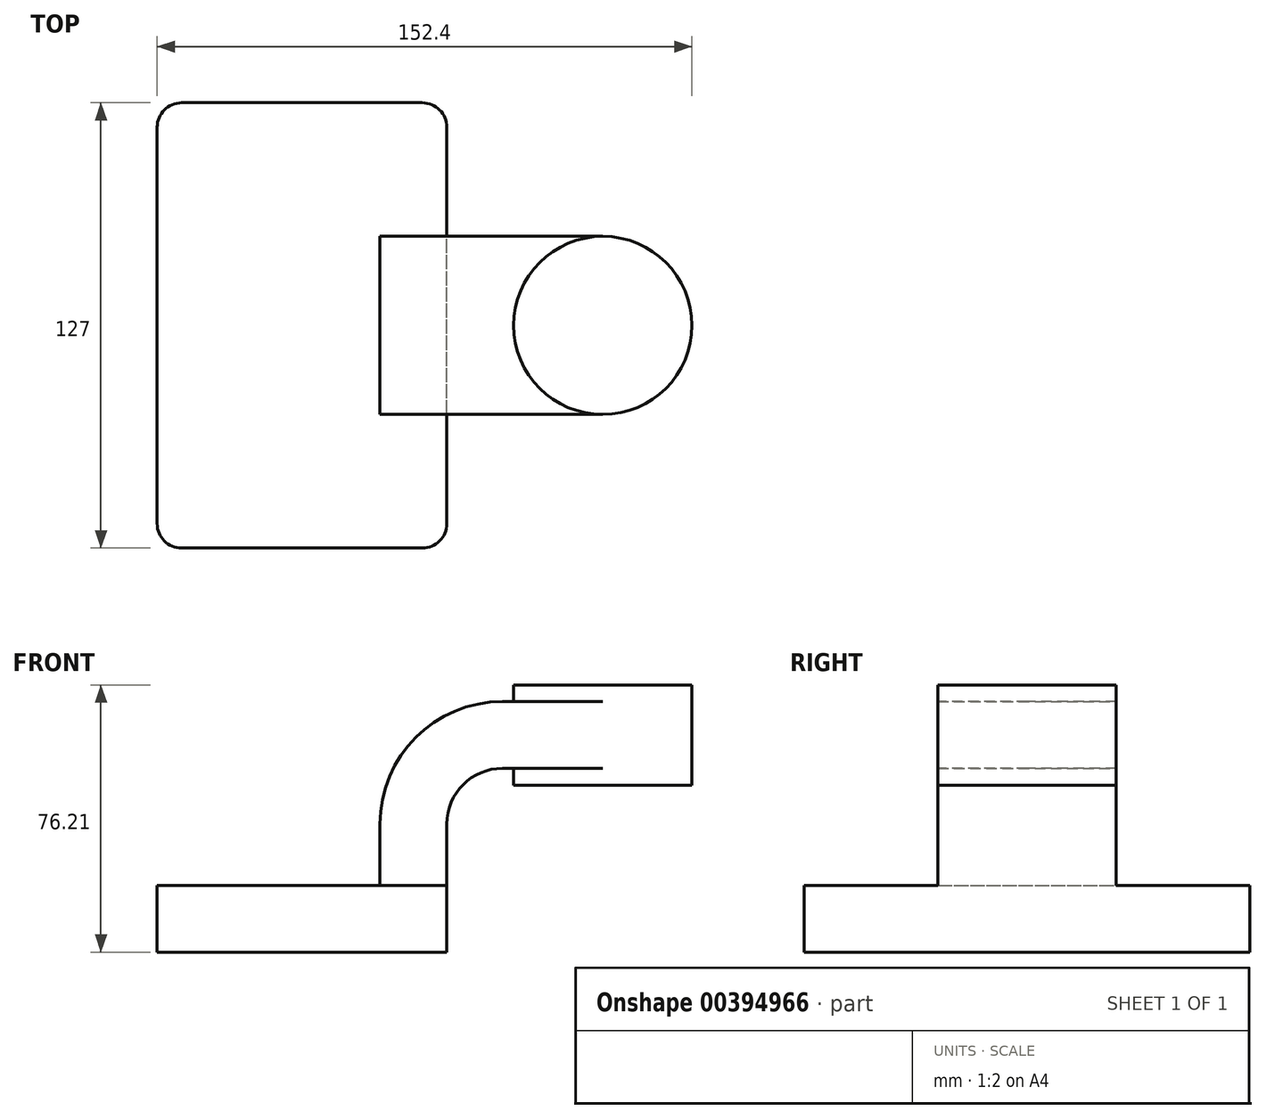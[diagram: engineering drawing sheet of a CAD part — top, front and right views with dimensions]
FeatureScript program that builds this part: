
annotation { "Feature Type Name" : "Feature", "Feature Type Description" : "" }
export const myFeature = defineFeature(function(context is Context, id is Id, definition is map)
    precondition{}
    {
        {
            var Q0;
            Q0=qCreatedBy(makeId("Front.planeOp"),FACE);
            var sketch = newSketch(context, id + "F0", { "sketchPlane" : qUnion([Q0])});
            skLineSegment(sketch, "E0.bottom", {"start": v(-41.28, 9.52) * mm, "end": v(41.27, 9.53) * mm});
            skLineSegment(sketch, "E0.top", {"start": v(-41.28, -9.52) * mm, "end": v(41.28, -9.52) * mm});
            skLineSegment(sketch, "E0.left", {"start": v(-41.28, 9.52) * mm, "end": v(-41.28, -9.53) * mm});
            skLineSegment(sketch, "E0.right", {"start": v(41.27, 9.53) * mm, "end": v(41.28, -9.52) * mm});
            skPoint(sketch, "E0.middle", {"position": v(0, 0) * mm});
            skLineSegment(sketch, "E1.bottom", {"start": v(60.32, 38.1) * mm, "end": v(111.12, 38.1) * mm});
            skLineSegment(sketch, "E1.top", {"start": v(60.32, 66.67) * mm, "end": v(111.12, 66.67) * mm});
            skLineSegment(sketch, "E1.left", {"start": v(60.32, 38.1) * mm, "end": v(60.32, 66.67) * mm});
            skLineSegment(sketch, "E1.right", {"start": v(111.12, 38.1) * mm, "end": v(111.12, 66.67) * mm});
            skPoint(sketch, "E1.middle", {"position": v(85.72, 52.39) * mm});
            skLineSegment(sketch, "E2", {"start": v(41.27, 9.53) * mm, "end": v(41.27, 27) * mm});
            skArc(sketch, "E3", {"start": v(41.27, 27) * mm, "mid": v(45.92, 38.23) * mm, "end": v(57.15, 42.88) * mm});
            skLineSegment(sketch, "E4", {"start": v(57.15, 42.88) * mm, "end": v(85.72, 42.88) * mm});
            skLineSegment(sketch, "E5.0", {"start": v(57.15, 61.93) * mm, "end": v(85.72, 61.93) * mm});
            skArc(sketch, "E5.1", {"start": v(22.22, 27) * mm, "mid": v(32.45, 51.7) * mm, "end": v(57.15, 61.93) * mm});
            skLineSegment(sketch, "E5.2", {"start": v(22.22, 9.53) * mm, "end": v(22.22, 27) * mm});
            skLineSegment(sketch, "E6", {"start": v(85.72, 38.1) * mm, "end": v(85.72, 66.67) * mm});
            skFitSpline(sketch, "E7", {"points": [v(-41.28, 9.53) * mm, v(57.15, 61.93) * mm], "startDerivative": vector(2.07, 128.38) * mm, "endDerivative": vector(129.28, -0.33) * mm});
            skSolve(sketch);
        }
        {
            var Q0;
            Q0=makeQuery(id+"F0.imprint","IMPRINT",FACE,{"disambiguationData":[TD([[makeQuery(id+"F0.imprint","IMPRINT",EDGE,{"derivedFrom":sQuery(id+"F0.wireOp",EDGE,"E0.top")}),1.0]])]});
            extrude(context, id + "F1", {"entities" : qUnion([Q0]), "endBound" : BoundingType.SYMMETRIC, "depth" : 127 * mm});
        }
        {
            var Q0;
            {var subQ1=sQuery(id+"F0.wireOp",EDGE,"E2");Q0=makeQuery(id+"F0.imprint","IMPRINT",FACE,{"disambiguationData":[TD([[makeQuery(id+"F0.imprint","IMPRINT",EDGE,{"derivedFrom":subQ1}),1.0]])]});}
            var Q1;
            {var subQ0=sQuery(id+"F0.wireOp",EDGE,"E4");var subQ1=sQuery(id+"F0.wireOp",EDGE,"E1.left");var subQ2=makeQuery(id+"F0.imprint","INTERSECT",VERTEX,{"derivedFrom":[subQ1,subQ0]});Q1=makeQuery(id+"F0.imprint","IMPRINT",FACE,{"disambiguationData":[TD([[makeQuery(id+"F0.imprint","IMPRINT",EDGE,{"disambiguationData":[TD([[subQ2,-1.0]])],"derivedFrom":subQ1}),-1.0]])]});}
            extrude(context, id + "F2", {"entities" : qUnion([Q0, Q1]), "operationType" : NewBodyOperationType.ADD, "endBound" : BoundingType.SYMMETRIC, "depth" : 50.8 * mm});
        }
        {
            var Q0;
            Q0=makeQuery(id+"F0.imprint","IMPRINT",FACE,{"disambiguationData":[TD([[makeQuery(id+"F0.imprint","IMPRINT",EDGE,{"derivedFrom":sQuery(id+"F0.wireOp",EDGE,"E5.1")}),1.0]])]});
            extrude(context, id + "F3", {"entities" : qUnion([Q0]), "operationType" : NewBodyOperationType.ADD, "endBound" : BoundingType.SYMMETRIC, "depth" : 15.88 * mm});
        }
        {
            var Q0;
            {var subQ0=sQuery(id+"F0.wireOp",EDGE,"E1.right");Q0=makeQuery(id+"F0.imprint","IMPRINT",FACE,{"disambiguationData":[TD([[makeQuery(id+"F0.imprint","IMPRINT",EDGE,{"derivedFrom":subQ0}),1.0]])]});}
            var Q1;
            Q1=sQuery(id+"F0.wireOp",EDGE,"E6");
            revolve(context, id + "F4", {"operationType" : NewBodyOperationType.ADD, "entities" : qUnion([Q0]), "axis" : qUnion([Q1]), "revolveType" : RevolveType.FULL});
        }
        {
            var Q0;
            Q0=makeQuery(id+"F1.opExtrude","CAP_EDGE",EDGE,{"disambiguationData":[OSD([sQuery(id+"F0.wireOp",EDGE,"E0.right")])],"isStart":true});
            var Q1;
            Q1=makeQuery(id+"F1.opExtrude","CAP_EDGE",EDGE,{"disambiguationData":[OSD([sQuery(id+"F0.wireOp",EDGE,"E0.right")])],"isStart":false});
            var Q2;
            Q2=makeQuery(id+"F1.opExtrude","CAP_EDGE",EDGE,{"disambiguationData":[OSD([sQuery(id+"F0.wireOp",EDGE,"E0.left")])],"isStart":false});
            var Q3;
            Q3=makeQuery(id+"F1.opExtrude","CAP_EDGE",EDGE,{"disambiguationData":[OSD([sQuery(id+"F0.wireOp",EDGE,"E0.left")])],"isStart":true});
            fillet(context, id + "F5", {"entities" : qUnion([Q0, Q1, Q2, Q3]), "radius" : 7 * mm, "tangentPropagation" : true, "allowEdgeOverflow" : false});
        }
    });
